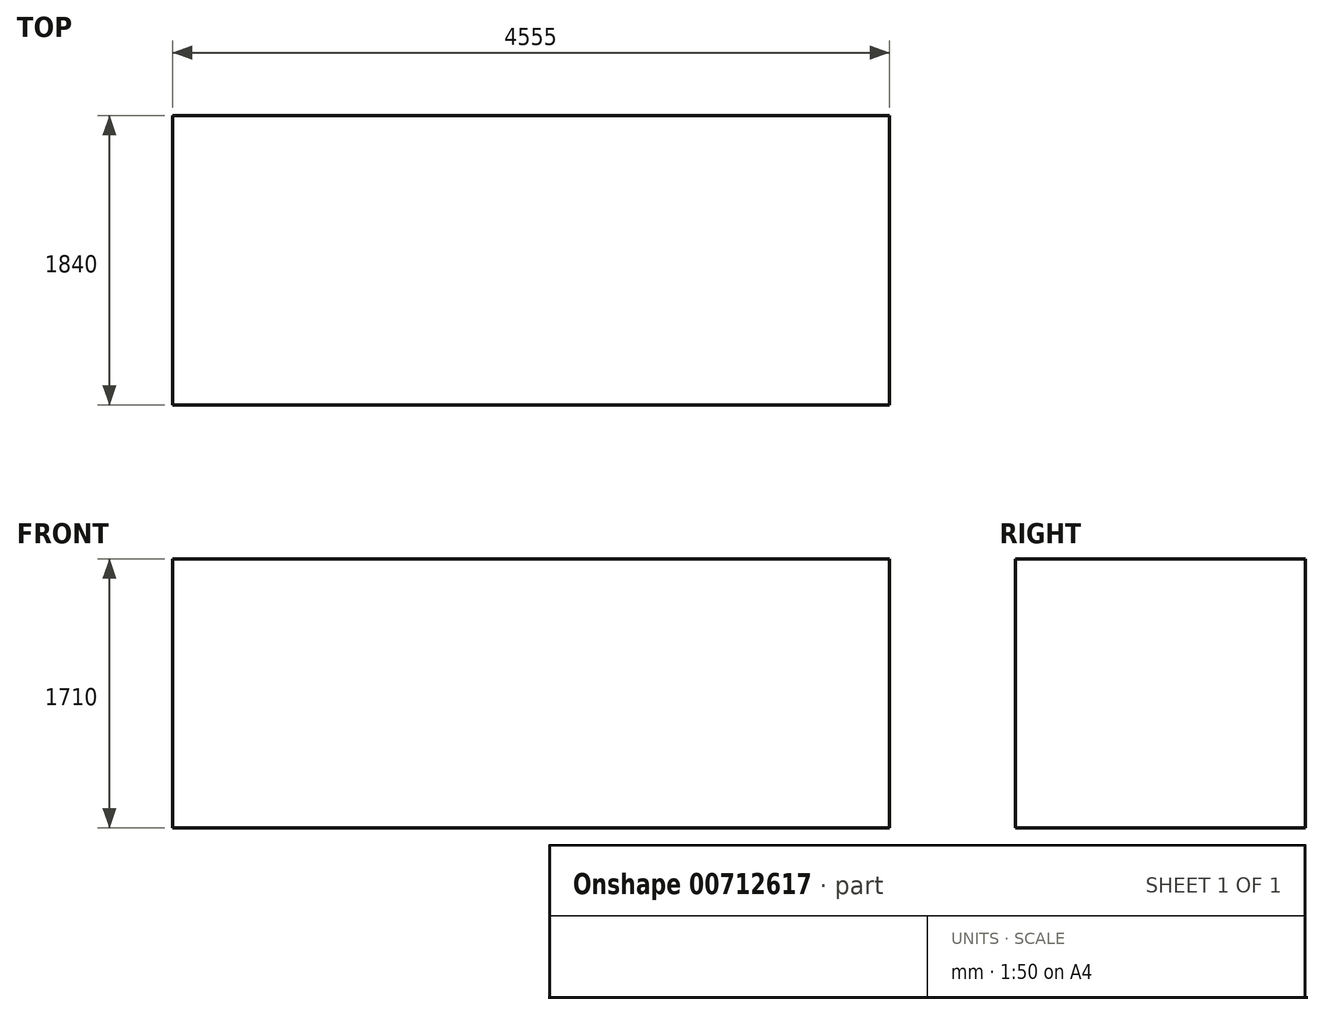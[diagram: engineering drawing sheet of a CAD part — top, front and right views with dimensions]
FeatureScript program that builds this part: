
annotation { "Feature Type Name" : "Feature", "Feature Type Description" : "" }
export const myFeature = defineFeature(function(context is Context, id is Id, definition is map)
    precondition{}
    {
        {
            var Q0;
            Q0=qCreatedBy(makeId("Top.planeOp"),FACE);
            var sketch = newSketch(context, id + "F0", { "sketchPlane" : qUnion([Q0])});
            skLineSegment(sketch, "E0.bottom", {"start": v(0, 0) * mm, "end": v(4555, 0) * mm});
            skLineSegment(sketch, "E0.top", {"start": v(0, 1840) * mm, "end": v(4555, 1840) * mm});
            skLineSegment(sketch, "E0.left", {"start": v(0, 0) * mm, "end": v(0, 1840) * mm});
            skLineSegment(sketch, "E0.right", {"start": v(4555, 0) * mm, "end": v(4555, 1840) * mm});
            skSolve(sketch);
        }
        {
            var Q0;
            Q0 = qSketchRegion(id + "F0", true);
            extrude(context, id + "F1", {"entities" : qUnion([Q0]), "depth" : 1710 * mm, "offsetDistance" : 25.4 * mm});
        }
    });
